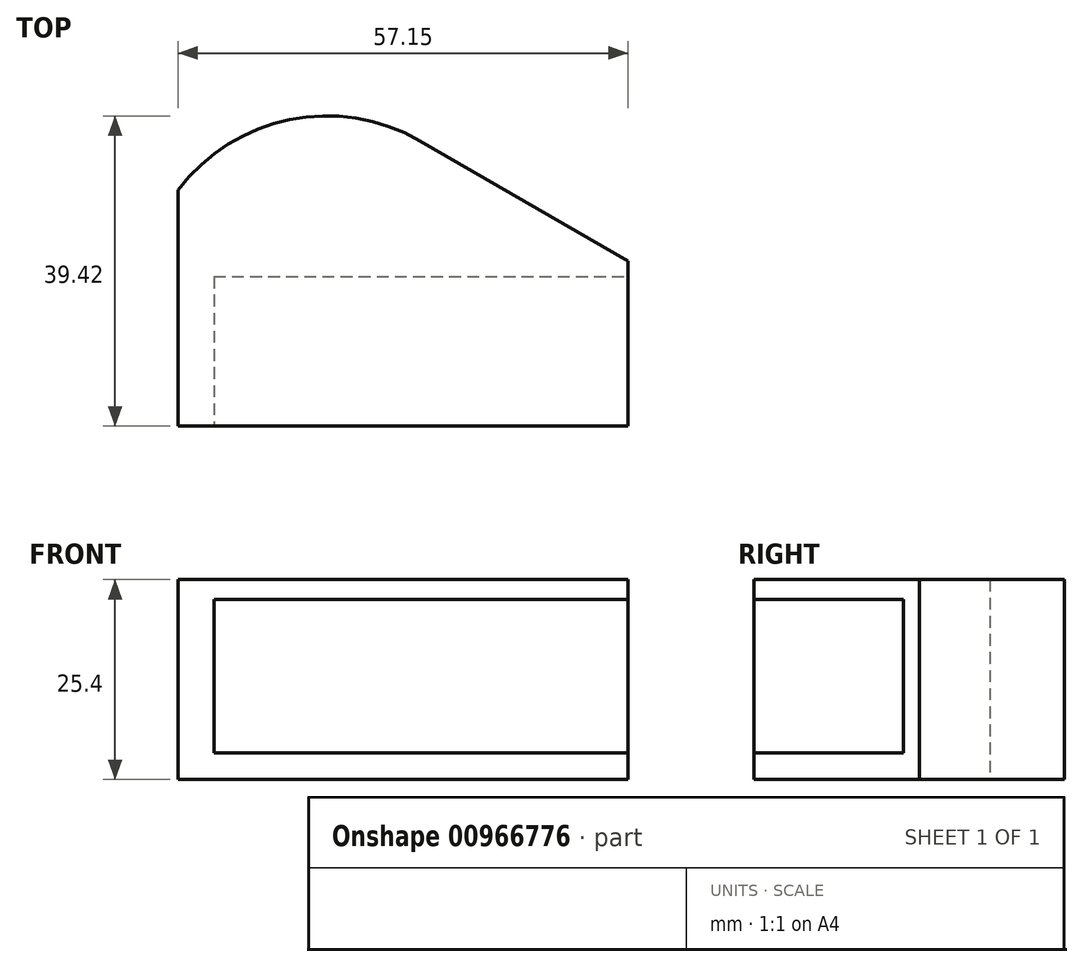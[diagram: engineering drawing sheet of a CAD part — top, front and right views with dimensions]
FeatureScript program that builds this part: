
annotation { "Feature Type Name" : "Feature", "Feature Type Description" : "" }
export const myFeature = defineFeature(function(context is Context, id is Id, definition is map)
    precondition{}
    {
        {
            var Q0;
            Q0=qCreatedBy(makeId("Top.planeOp"),FACE);
            var sketch = newSketch(context, id + "F0", { "sketchPlane" : qUnion([Q0])});
            skLineSegment(sketch, "E0", {"start": v(0, 0) * mm, "end": v(57.15, 0) * mm});
            skLineSegment(sketch, "E1", {"start": v(57.15, 0) * mm, "end": v(57.15, 21) * mm});
            skLineSegment(sketch, "E2", {"start": v(0, 0) * mm, "end": v(0, 30) * mm});
            skLineSegment(sketch, "E3", {"start": v(57.15, 21) * mm, "end": v(30.75, 36.24) * mm});
            skArc(sketch, "E4", {"start": v(30.75, 36.24) * mm, "mid": v(14.2, 38.94) * mm, "end": v(0, 30) * mm});
            skSolve(sketch);
        }
        {
            var Q0;
            Q0 = qSketchRegion(id + "F0", true);
            extrude(context, id + "F1", {"entities" : qUnion([Q0]), "depth" : (1 * 25.4) * mm, "offsetDistance" : 25 * mm});
        }
        {
            var Q0;
            Q0=makeQuery(id+"F1.opExtrude","SWEPT_FACE",FACE,{"disambiguationData":[OSD([sQuery(id+"F0.wireOp",EDGE,"E0")])]});
            var sketch = newSketch(context, id + "F2", { "sketchPlane" : qUnion([Q0])});
            skLineSegment(sketch, "E5.bottom", {"start": v(4.55, 3.4) * mm, "end": v(57.15, 3.4) * mm});
            skLineSegment(sketch, "E5.top", {"start": v(4.55, 22.9) * mm, "end": v(57.15, 22.9) * mm});
            skLineSegment(sketch, "E5.left", {"start": v(4.55, 3.4) * mm, "end": v(4.55, 22.9) * mm});
            skLineSegment(sketch, "E5.right", {"start": v(57.15, 3.4) * mm, "end": v(57.15, 22.9) * mm});
            skSolve(sketch);
        }
        {
            var Q0;
            Q0 = qSketchRegion(id + "F2", true);
            extrude(context, id + "F3", {"entities" : qUnion([Q0]), "operationType" : NewBodyOperationType.REMOVE, "oppositeDirection" : true, "depth" : 19 * mm, "offsetDistance" : 25 * mm});
        }
    });
